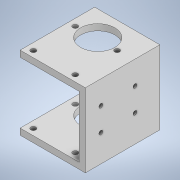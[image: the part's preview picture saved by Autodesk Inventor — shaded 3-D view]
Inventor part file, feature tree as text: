
AUTODESK INVENTOR PART (.ipt)
format: ipt  version: 2022 (Build 260153000, 153)  size: 163,328 bytes
history: native  units: mm
features: sketch x5, hole x3, extrude x2, other x1
ambient origin geometry x8: Origin, YZ Plane, XZ Plane, XY Plane, X Axis, Y Axis, Z Axis, Center Point
bodies: Body1 (feature_tree)
feature tree (11):
  other  "ソリッド1"
  extrude  "押し出し1"  Depth=48.0mm
  extrude  "押し出し2"  Depth=42.0mm
  hole  "穴1"  [1 undecoded]
  hole  "穴2"  [1 undecoded]
  hole  "穴4"  [1 undecoded]
  sketch  "スケッチ1"
  sketch  "スケッチ2"
  sketch  "スケッチ3"
  sketch  "スケッチ4"
  sketch  "スケッチ6"
note: 3 required parameter values undecoded (feature->parameter linkage not recoverable at this tier; creation-order binding heuristic only, values carry confidence <= 0.55)
